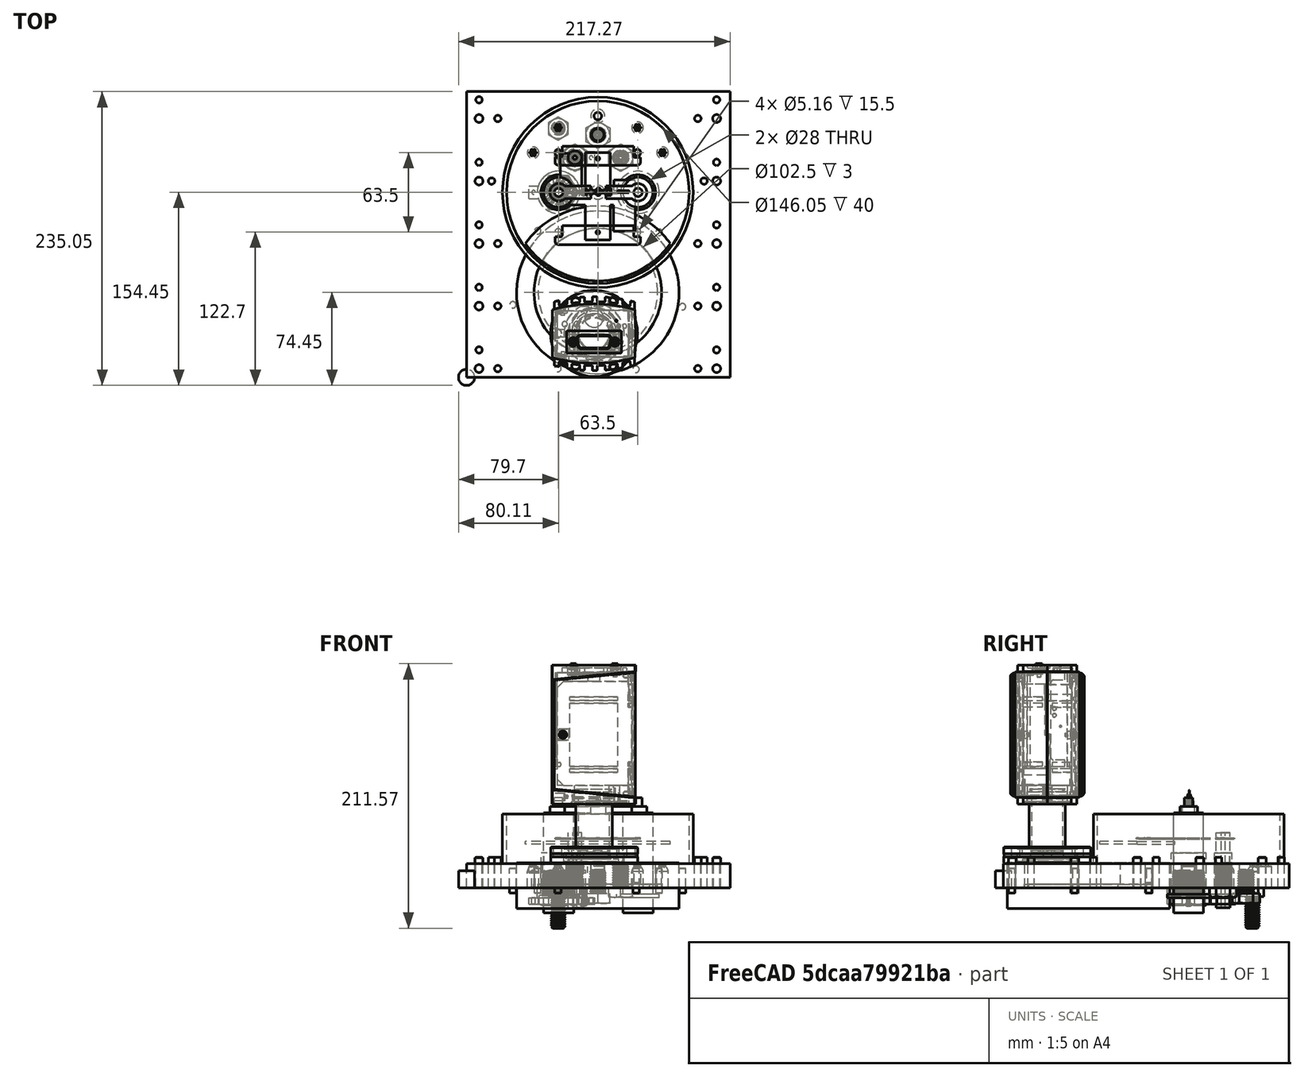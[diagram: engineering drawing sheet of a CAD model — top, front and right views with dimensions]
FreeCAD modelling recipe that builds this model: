
FCSTD DOCUMENT  (FreeCAD 0.17R13509 (Git))
Label: chamber_RF_new_feeds_sim
License: All rights reserved
LicenseURL: http://en.wikipedia.org/wiki/All_rights_reserved
objects: Part::Cylinder×125, Part::MultiFuse×48, Part::Box×24, Part::Cut×15, Part::Feature×8, Part::Fillet×6, Part::FeaturePython×5, Part::Sphere×4, Part::MultiCommon×2, Part::Cone×2
note: 239 computed .brp shape members not serialized (recipe doc carries the construction recipe); baked Part::Feature solids carry a one-line shape summary decoded from their .brp

FEATURE [Part::Box] Box  label="BasePlate"
  AttacherType = Attacher::AttachEngine3D
  Height = 19.5
  Length = 210.82
  Width = 228.6
  expr: Length = 8.3000000000000007 * 25.399999999999999
  expr: Width = 9 * 25.399999999999999
FEATURE [Part::Cylinder] Cylinder  label="Flange"
  Angle = 360
  AttacherType = Attacher::AttachEngine3D
  Height = 20
  Placement = pos=(105,68,0) rot=(0,0,1;0rad)
  Radius = 65
  expr: Placement.Base.x = 210 / 2
  expr: Radius = 130 / 2
FEATURE [Part::Cylinder] Cylinder001  label="TurboPumpInlet"
  Angle = 360
  AttacherType = Attacher::AttachEngine3D
  Height = 20
  Placement = pos=(105,68,0) rot=(0,0,1;0rad)
  Radius = 51
  expr: Placement.Base.x = 210 / 2
  expr: Radius = 102 / 2
FEATURE [Part::Cylinder] Cylinder002  label="ChamberWall"
  Angle = 360
  AttacherType = Attacher::AttachEngine3D
  Height = 40
  Placement = pos=(105,148,0) rot=(0,0,1;0rad)
  Radius = 76.2
  expr: Placement.Base.x = 210 / 2
  expr: Radius = 3 * 25.399999999999999
FEATURE [Part::Cylinder] Cylinder003  label="TurboPump"
  Angle = 360
  AttacherType = Attacher::AttachEngine3D
  Height = 16.4
  Placement = pos=(105,68,-16.4) rot=(0,0,1;0rad)
  Radius = 65
  expr: Placement.Base.x = 210 / 2
  expr: Radius = 130 / 2
FEATURE [Part::Cylinder] Cylinder004  label="Chamber001"
  Angle = 360
  AttacherType = Attacher::AttachEngine3D
  Height = 20
  Placement = pos=(105,148,0) rot=(0,0,1;0rad)
  Radius = 70.0875
  expr: Placement.Base.x = 210 / 2
  expr: Radius = 5.5625 * 25.199999999999999 / 2
FEATURE [Part::Cylinder] Cylinder005
  Angle = 360
  AttacherType = Attacher::AttachEngine3D
  Height = 20
  Placement = pos=(105,68,0) rot=(0,0,1;0rad)
  Radius = 51
  expr: Placement.Base.x = 210 / 2
  expr: Radius = 102 / 2
FEATURE [Part::MultiCommon] Common  label="Inlet"
  Shapes = -> [Cylinder004,Cylinder005]
FEATURE [Part::Cylinder] Cylinder012  label="Threaded"
  Angle = 360
  AttacherType = Attacher::AttachEngine3D
  Height = 19.5
  Placement = pos=(36.025,58.5,-4) rot=(0,0,1;0rad)
  Radius = 2.57969
  expr: Placement.Base.x = 105 - 68.674999999999997 - 0.29999999999999999
  expr: Radius = 13 / 64 * 25.399999999999999 / 2
FEATURE [Part::MultiFuse] Fusion
  Shapes = -> [Cylinder003,Cylinder001]
FEATURE [Part::Cylinder] Cylinder008  label="ChamberWall001"
  Angle = 360
  AttacherType = Attacher::AttachEngine3D
  Height = 40
  Placement = pos=(105,148,0) rot=(0,0,1;0rad)
  Radius = 73.025
  expr: Placement.Base.x = 210 / 2
  expr: Radius = (3 - 0.125) * 25.399999999999999
FEATURE [Part::Cut] Cut  label="ChamberWall002"
  Base = -> Cylinder002
  Placement = pos=(0,0,19) rot=(0,0,1;0rad)
  Tool = -> Cylinder008
FEATURE [Part::Cylinder] Cylinder013  label="Threaded001"
  Angle = 360
  AttacherType = Attacher::AttachEngine3D
  Height = 19.5
  Placement = pos=(136.75,179.75,4) rot=(0,0,1;0rad)
  Radius = 2.57969
  expr: Placement.Base.x = 105 + 31.75
  expr: Placement.Base.y = 148 + 31.75
  expr: Radius = 13 / 64 * 25.399999999999999 / 2
FEATURE [Part::Cylinder] Cylinder014  label="Threaded002"
  Angle = 360
  AttacherType = Attacher::AttachEngine3D
  Height = 19.5
  Placement = pos=(73.25,179.75,4) rot=(0,0,1;0rad)
  Radius = 2.57969
  expr: Placement.Base.x = 105 - 31.75
  expr: Placement.Base.y = 148 + 31.75
  expr: Radius = 13 / 64 * 25.399999999999999 / 2
FEATURE [Part::Cylinder] Cylinder015  label="Threaded003"
  Angle = 360
  AttacherType = Attacher::AttachEngine3D
  Height = 23.5
  Placement = pos=(73.25,116.25,4) rot=(0,0,1;0rad)
  Radius = 2.57969
  expr: Placement.Base.x = 105 - 31.75
  expr: Placement.Base.y = 148 - 31.75
  expr: Radius = 13 / 64 * 25.399999999999999 / 2
FEATURE [Part::Cylinder] Cylinder016  label="Threaded004"
  Angle = 360
  AttacherType = Attacher::AttachEngine3D
  Height = 23.5
  Placement = pos=(136.75,116.25,4) rot=(0,0,1;0rad)
  Radius = 2.57969
  expr: Placement.Base.x = 105 + 31.75
  expr: Placement.Base.y = 148 - 31.75
  expr: Radius = 13 / 64 * 25.399999999999999 / 2
FEATURE [Part::MultiFuse] Fusion003  label="Risers"
  Shapes = -> [Cylinder016,Cylinder015,Cylinder014,Cylinder013]
FEATURE [Part::Cylinder] Cylinder017  label="Unthreaded"
  Angle = 360
  AttacherType = Attacher::AttachEngine3D
  Height = 24
  Placement = pos=(10,10,0) rot=(0,0,1;0rad)
  Radius = 3.175
FEATURE [Part::FeaturePython] Array  label="TurboMounts"  # Draft array (typed FeaturePython)
  Angle = 270
  ArrayType = 1
  Axis = (0,0,1)
  Base = -> Cylinder012
  Center = (0,0,0)
  Fuse = false
  IntervalAxis = (0,0,0)
  IntervalX = (1,0,0)
  IntervalY = (0,1,0)
  IntervalZ = (0,0,0)
  NumberPolar = 6
  NumberX = 2
  NumberY = 2
  NumberZ = 1
  Placement = pos=(105,68,0) rot=(0,0,1;1.32645rad)
FEATURE [Part::Cylinder] Cylinder018  label="Threaded005"
  Angle = 360
  AttacherType = Attacher::AttachEngine3D
  Height = 24.5
  Placement = pos=(25,10,0) rot=(0,0,1;0rad)
  Radius = 2.57969
FEATURE [Part::Cylinder] Cylinder019  label="Unthreaded001"
  Angle = 360
  AttacherType = Attacher::AttachEngine3D
  Height = 24
  Placement = pos=(10,10,0) rot=(0,0,1;0rad)
  Radius = 3.175
FEATURE [Part::Cylinder] Cylinder020  label="Threaded006"
  Angle = 360
  AttacherType = Attacher::AttachEngine3D
  Height = 24.5
  Placement = pos=(-5,10,0) rot=(0,0,1;0rad)
  Radius = 2.57969
FEATURE [Part::Cylinder] Cylinder021  label="Threaded007"
  Angle = 360
  AttacherType = Attacher::AttachEngine3D
  Height = 24.5
  Placement = pos=(10,25,0) rot=(0,0,1;0rad)
  Radius = 2.57969
FEATURE [Part::MultiFuse] Fusion004  label="MountSet1"
  Shapes = -> [Cylinder021,Cylinder018,Cylinder017]
FEATURE [Part::Cylinder] Cylinder022  label="Threaded008"
  Angle = 360
  AttacherType = Attacher::AttachEngine3D
  Height = 24.5
  Placement = pos=(10,25,0) rot=(0,0,1;0rad)
  Radius = 2.57969
FEATURE [Part::MultiFuse] Fusion005  label="MountSet2"
  Placement = pos=(190,0,0) rot=(0,0,1;0rad)
  Shapes = -> [Cylinder022,Cylinder019,Cylinder020]
FEATURE [Part::MultiFuse] Fusion006  label="MountBar"
  Shapes = -> [Fusion005,Fusion004]
FEATURE [Part::Cylinder] Cylinder023  label="Unthreaded002"
  Angle = 360
  AttacherType = Attacher::AttachEngine3D
  Height = 24
  Placement = pos=(10,10,0) rot=(0,0,1;0rad)
  Radius = 3.175
FEATURE [Part::Cylinder] Cylinder024  label="Threaded009"
  Angle = 360
  AttacherType = Attacher::AttachEngine3D
  Height = 24.5
  Placement = pos=(25,10,0) rot=(0,0,1;0rad)
  Radius = 2.57969
FEATURE [Part::Cylinder] Cylinder025  label="Unthreaded003"
  Angle = 360
  AttacherType = Attacher::AttachEngine3D
  Height = 24
  Placement = pos=(10,10,0) rot=(0,0,1;0rad)
  Radius = 3.175
FEATURE [Part::Cylinder] Cylinder026  label="Threaded010"
  Angle = 360
  AttacherType = Attacher::AttachEngine3D
  Height = 24.5
  Placement = pos=(-5,10,0) rot=(0,0,1;0rad)
  Radius = 2.57969
FEATURE [Part::Cylinder] Cylinder027  label="Threaded011"
  Angle = 360
  AttacherType = Attacher::AttachEngine3D
  Height = 24.5
  Placement = pos=(10,25,0) rot=(0,0,1;0rad)
  Radius = 2.57969
FEATURE [Part::MultiFuse] Fusion007  label="MountSet003"
  Shapes = -> [Cylinder027,Cylinder024,Cylinder023]
FEATURE [Part::Cylinder] Cylinder028  label="Threaded012"
  Angle = 360
  AttacherType = Attacher::AttachEngine3D
  Height = 24.5
  Placement = pos=(10,25,0) rot=(0,0,1;0rad)
  Radius = 2.57969
FEATURE [Part::MultiFuse] Fusion008  label="MountSet004"
  Placement = pos=(190,0,0) rot=(0,0,1;0rad)
  Shapes = -> [Cylinder028,Cylinder025,Cylinder026]
FEATURE [Part::MultiFuse] Fusion009  label="MountBar001"
  Placement = pos=(0,50,0) rot=(0,0,1;0rad)
  Shapes = -> [Fusion008,Fusion007]
FEATURE [Part::Cylinder] Cylinder029  label="Unthreaded004"
  Angle = 360
  AttacherType = Attacher::AttachEngine3D
  Height = 24
  Placement = pos=(10,10,0) rot=(0,0,1;0rad)
  Radius = 3.175
FEATURE [Part::Cylinder] Cylinder030  label="Threaded013"
  Angle = 360
  AttacherType = Attacher::AttachEngine3D
  Height = 24.5
  Placement = pos=(25,10,0) rot=(0,0,1;0rad)
  Radius = 2.57969
FEATURE [Part::Cylinder] Cylinder031  label="Unthreaded005"
  Angle = 360
  AttacherType = Attacher::AttachEngine3D
  Height = 24
  Placement = pos=(10,10,0) rot=(0,0,1;0rad)
  Radius = 3.175
FEATURE [Part::Cylinder] Cylinder032  label="Threaded014"
  Angle = 360
  AttacherType = Attacher::AttachEngine3D
  Height = 24.5
  Placement = pos=(-5,10,0) rot=(0,0,1;0rad)
  Radius = 2.57969
FEATURE [Part::Cylinder] Cylinder033  label="Threaded015"
  Angle = 360
  AttacherType = Attacher::AttachEngine3D
  Height = 24.5
  Placement = pos=(10,25,0) rot=(0,0,1;0rad)
  Radius = 2.57969
FEATURE [Part::MultiFuse] Fusion010  label="MountSet005"
  Shapes = -> [Cylinder033,Cylinder030,Cylinder029]
FEATURE [Part::Cylinder] Cylinder034  label="Threaded016"
  Angle = 360
  AttacherType = Attacher::AttachEngine3D
  Height = 24.5
  Placement = pos=(10,25,0) rot=(0,0,1;0rad)
  Radius = 2.57969
FEATURE [Part::MultiFuse] Fusion011  label="MountSet006"
  Placement = pos=(190,0,0) rot=(0,0,1;0rad)
  Shapes = -> [Cylinder034,Cylinder031,Cylinder032]
FEATURE [Part::MultiFuse] Fusion012  label="MountBar002"
  Placement = pos=(0,100,0) rot=(0,0,1;0rad)
  Shapes = -> [Fusion011,Fusion010]
FEATURE [Part::Cylinder] Cylinder035  label="Unthreaded006"
  Angle = 360
  AttacherType = Attacher::AttachEngine3D
  Height = 24
  Placement = pos=(10,10,0) rot=(0,0,1;0rad)
  Radius = 3.175
FEATURE [Part::Cylinder] Cylinder036  label="Threaded017"
  Angle = 360
  AttacherType = Attacher::AttachEngine3D
  Height = 24.5
  Placement = pos=(20,10,0) rot=(0,0,1;0rad)
  Radius = 2.57969
FEATURE [Part::Cylinder] Cylinder037  label="Unthreaded007"
  Angle = 360
  AttacherType = Attacher::AttachEngine3D
  Height = 24
  Placement = pos=(10,10,0) rot=(0,0,1;0rad)
  Radius = 3.175
FEATURE [Part::Cylinder] Cylinder038  label="Threaded018"
  Angle = 360
  AttacherType = Attacher::AttachEngine3D
  Height = 24.5
  Placement = pos=(0,10,0) rot=(0,0,1;0rad)
  Radius = 2.57969
FEATURE [Part::Cylinder] Cylinder039  label="Threaded019"
  Angle = 360
  AttacherType = Attacher::AttachEngine3D
  Height = 24.5
  Placement = pos=(10,25,0) rot=(0,0,1;0rad)
  Radius = 2.57969
FEATURE [Part::MultiFuse] Fusion013  label="MountSet007"
  Shapes = -> [Cylinder039,Cylinder036,Cylinder035]
FEATURE [Part::Cylinder] Cylinder040  label="Threaded020"
  Angle = 360
  AttacherType = Attacher::AttachEngine3D
  Height = 24.5
  Placement = pos=(10,25,0) rot=(0,0,1;0rad)
  Radius = 2.57969
FEATURE [Part::MultiFuse] Fusion014  label="MountSet008"
  Placement = pos=(190,0,0) rot=(0,0,1;0rad)
  Shapes = -> [Cylinder040,Cylinder037,Cylinder038]
FEATURE [Part::MultiFuse] Fusion015  label="MountBar003"
  Placement = pos=(0,150,0) rot=(0,0,1;0rad)
  Shapes = -> [Fusion014,Fusion013]
FEATURE [Part::Cylinder] Cylinder041  label="Unthreaded008"
  Angle = 360
  AttacherType = Attacher::AttachEngine3D
  Height = 24
  Placement = pos=(10,10,0) rot=(0,0,1;0rad)
  Radius = 3.175
FEATURE [Part::Cylinder] Cylinder042  label="Threaded021"
  Angle = 360
  AttacherType = Attacher::AttachEngine3D
  Height = 24.5
  Placement = pos=(25,10,0) rot=(0,0,1;0rad)
  Radius = 2.57969
FEATURE [Part::Cylinder] Cylinder043  label="Unthreaded009"
  Angle = 360
  AttacherType = Attacher::AttachEngine3D
  Height = 24
  Placement = pos=(10,10,0) rot=(0,0,1;0rad)
  Radius = 3.175
FEATURE [Part::Cylinder] Cylinder044  label="Threaded022"
  Angle = 360
  AttacherType = Attacher::AttachEngine3D
  Height = 24.5
  Placement = pos=(-5,10,0) rot=(0,0,1;0rad)
  Radius = 2.57969
FEATURE [Part::Cylinder] Cylinder045  label="Threaded023"
  Angle = 360
  AttacherType = Attacher::AttachEngine3D
  Height = 24.5
  Placement = pos=(10,25,0) rot=(0,0,1;0rad)
  Radius = 2.57969
FEATURE [Part::MultiFuse] Fusion016  label="MountSet009"
  Shapes = -> [Cylinder045,Cylinder042,Cylinder041]
FEATURE [Part::Cylinder] Cylinder046  label="Threaded024"
  Angle = 360
  AttacherType = Attacher::AttachEngine3D
  Height = 24.5
  Placement = pos=(10,25,0) rot=(0,0,1;0rad)
  Radius = 2.57969
FEATURE [Part::MultiFuse] Fusion017  label="MountSet010"
  Placement = pos=(190,0,0) rot=(0,0,1;0rad)
  Shapes = -> [Cylinder046,Cylinder043,Cylinder044]
FEATURE [Part::MultiFuse] Fusion018  label="MountBar004"
  Placement = pos=(0,200,0) rot=(0,0,1;0rad)
  Shapes = -> [Fusion017,Fusion016]
FEATURE [Part::MultiFuse] Fusion019  label="MountSet"
  Placement = pos=(0,-3,0) rot=(0,0,1;0rad)
  Shapes = -> [Fusion018,Fusion015,Fusion012,Fusion009,Fusion006]
FEATURE [Part::Cylinder] Cylinder048  label="NPT1"
  Angle = 360
  AttacherType = Attacher::AttachEngine3D
  Height = 18
  Placement = pos=(105,148,0) rot=(0,0,1;0rad)
  Radius = 5.55625
  expr: Radius = 7 / 16 * 25.399999999999999 / 2
FEATURE [Part::Cylinder] Cylinder049  label="WireFT1"
  Angle = 360
  AttacherType = Attacher::AttachEngine3D
  Height = 13
  Radius = 4.56406
  expr: Radius = 23 / 64 * 25.399999999999999 / 2
FEATURE [Part::Cylinder] Cylinder051  label="Flange001"
  Angle = 360
  AttacherType = Attacher::AttachEngine3D
  Height = 3
  Placement = pos=(105,68,0) rot=(0,0,1;0rad)
  Radius = 51.25
  expr: Placement.Base.x = 210 / 2
  expr: Radius = 102.5 / 2
FEATURE [Part::Cylinder] Cylinder052  label="Flange002"
  Angle = 360
  AttacherType = Attacher::AttachEngine3D
  Height = 3
  Placement = pos=(105,68,0) rot=(0,0,1;0rad)
  Radius = 47.75
  expr: Placement.Base.x = 210 / 2
  expr: Radius = 51.25 - 3.5
FEATURE [Part::Cut] Cut001  label="CenteringRingGroove"
  Base = -> Cylinder051
  Tool = -> Cylinder052
FEATURE [Part::Cylinder] Cylinder053  label="NPT002"
  Angle = 360
  AttacherType = Attacher::AttachEngine3D
  Height = 17
  Placement = pos=(105,209,0) rot=(0,0,1;0rad)
  Radius = 5.55625
  expr: Radius = 7 / 16 * 25.399999999999999 / 2
FEATURE [Part::Cylinder] Cylinder054  label="WireHole"
  Angle = 360
  AttacherType = Attacher::AttachEngine3D
  Height = 28
  Placement = pos=(2,0,0) rot=(0,0,1;0rad)
  Radius = 0.79375
FEATURE [Part::FeaturePython] Array001  # Draft array (typed FeaturePython)
  Angle = 360
  ArrayType = 1
  Axis = (0,0,1)
  Base = -> Cylinder054
  Center = (0,0,0)
  Fuse = false
  IntervalAxis = (0,0,0)
  IntervalX = (1,0,0)
  IntervalY = (0,1,0)
  IntervalZ = (0,0,0)
  NumberPolar = 6
  NumberX = 2
  NumberY = 2
  NumberZ = 1
FEATURE [Part::Cylinder] Cylinder056  label="WireHole001"
  Angle = 360
  AttacherType = Attacher::AttachEngine3D
  Height = 28
  Radius = 0.79375
FEATURE [Part::MultiFuse] Fusion020  label="WireFT_Holes"
  Shapes = -> [Cylinder056,Array001]
FEATURE [Part::Cylinder] Cylinder058  label="WireFT003"
  Angle = 360
  AttacherType = Attacher::AttachEngine3D
  Height = 13
  Radius = 4.56406
  expr: Radius = 23 / 64 * 25.399999999999999 / 2
FEATURE [Part::Cylinder] Cylinder059  label="WireHole002"
  Angle = 360
  AttacherType = Attacher::AttachEngine3D
  Height = 28
  Placement = pos=(2,0,0) rot=(0,0,1;0rad)
  Radius = 0.79375
FEATURE [Part::FeaturePython] Array002  # Draft array (typed FeaturePython)
  Angle = 360
  ArrayType = 1
  Axis = (0,0,1)
  Base = -> Cylinder059
  Center = (0,0,0)
  Fuse = false
  IntervalAxis = (0,0,0)
  IntervalX = (1,0,0)
  IntervalY = (0,1,0)
  IntervalZ = (0,0,0)
  NumberPolar = 6
  NumberX = 2
  NumberY = 2
  NumberZ = 1
FEATURE [Part::Cylinder] Cylinder060  label="WireHole003"
  Angle = 360
  AttacherType = Attacher::AttachEngine3D
  Height = 28
  Radius = 0.79375
FEATURE [Part::MultiFuse] Fusion022  label="WireFT_Holes001"
  Shapes = -> [Cylinder060,Array002]
FEATURE [Part::Sphere] Sphere  label="Compression"
  Angle1 = -90
  Angle2 = 90
  Angle3 = 360
  AttacherType = Attacher::AttachEngine3D
  Placement = pos=(0,0,13) rot=(0,0,1;0rad)
  Radius = 4.56
FEATURE [Part::MultiFuse] Fusion024  label="WireFT"
  Placement = pos=(53.25,179.75,0) rot=(0,0,1;0rad)
  Shapes = -> [Sphere,Fusion020,Cylinder049]
  expr: Placement.Base.x = 73.25 - 20
FEATURE [Part::Sphere] Sphere001  label="Compression001"
  Angle1 = -90
  Angle2 = 90
  Angle3 = 360
  AttacherType = Attacher::AttachEngine3D
  Placement = pos=(0,0,13) rot=(0,0,1;0rad)
  Radius = 4.56
FEATURE [Part::MultiFuse] Fusion025  label="WireFT004"
  Placement = pos=(73.25,199.75,0) rot=(0,0,1;0rad)
  Shapes = -> [Cylinder058,Fusion022,Sphere001]
  expr: Placement.Base.y = 179.75 + 20
FEATURE [Part::Cylinder] Cylinder061  label="WireFT005"
  Angle = 360
  AttacherType = Attacher::AttachEngine3D
  Height = 13
  Radius = 4.56406
  expr: Radius = 23 / 64 * 25.399999999999999 / 2
FEATURE [Part::Cylinder] Cylinder062  label="WireHole004"
  Angle = 360
  AttacherType = Attacher::AttachEngine3D
  Height = 28
  Placement = pos=(2,0,0) rot=(0,0,1;0rad)
  Radius = 0.79375
FEATURE [Part::FeaturePython] Array003  # Draft array (typed FeaturePython)
  Angle = 360
  ArrayType = 1
  Axis = (0,0,1)
  Base = -> Cylinder062
  Center = (0,0,0)
  Fuse = false
  IntervalAxis = (0,0,0)
  IntervalX = (1,0,0)
  IntervalY = (0,1,0)
  IntervalZ = (0,0,0)
  NumberPolar = 6
  NumberX = 2
  NumberY = 2
  NumberZ = 1
FEATURE [Part::Cylinder] Cylinder063  label="WireHole005"
  Angle = 360
  AttacherType = Attacher::AttachEngine3D
  Height = 28
  Radius = 0.79375
FEATURE [Part::MultiFuse] Fusion026  label="WireFT_Holes002"
  Shapes = -> [Cylinder063,Array003]
FEATURE [Part::Sphere] Sphere002  label="Compression002"
  Angle1 = -90
  Angle2 = 90
  Angle3 = 360
  AttacherType = Attacher::AttachEngine3D
  Placement = pos=(0,0,13) rot=(0,0,1;0rad)
  Radius = 4.56
FEATURE [Part::MultiFuse] Fusion027  label="WireFT006"
  Placement = pos=(136.75,199.75,0) rot=(0,0,1;0rad)
  Shapes = -> [Cylinder061,Fusion026,Sphere002]
  expr: Placement.Base.y = 179.75 + 20
FEATURE [Part::Cylinder] Cylinder064  label="WireFT007"
  Angle = 360
  AttacherType = Attacher::AttachEngine3D
  Height = 13
  Radius = 4.56406
  expr: Radius = 23 / 64 * 25.399999999999999 / 2
FEATURE [Part::Cylinder] Cylinder065  label="WireHole006"
  Angle = 360
  AttacherType = Attacher::AttachEngine3D
  Height = 28
  Placement = pos=(2,0,0) rot=(0,0,1;0rad)
  Radius = 0.79375
FEATURE [Part::FeaturePython] Array004  # Draft array (typed FeaturePython)
  Angle = 360
  ArrayType = 1
  Axis = (0,0,1)
  Base = -> Cylinder065
  Center = (0,0,0)
  Fuse = false
  IntervalAxis = (0,0,0)
  IntervalX = (1,0,0)
  IntervalY = (0,1,0)
  IntervalZ = (0,0,0)
  NumberPolar = 6
  NumberX = 2
  NumberY = 2
  NumberZ = 1
FEATURE [Part::Cylinder] Cylinder066  label="WireHole007"
  Angle = 360
  AttacherType = Attacher::AttachEngine3D
  Height = 28
  Radius = 0.79375
FEATURE [Part::MultiFuse] Fusion028  label="WireFT_Holes003"
  Shapes = -> [Cylinder066,Array004]
FEATURE [Part::Sphere] Sphere003  label="Compression003"
  Angle1 = -90
  Angle2 = 90
  Angle3 = 360
  AttacherType = Attacher::AttachEngine3D
  Placement = pos=(0,0,13) rot=(0,0,1;0rad)
  Radius = 4.56
FEATURE [Part::MultiFuse] Fusion029  label="WireFT008"
  Placement = pos=(156.75,179.75,0) rot=(0,0,1;0rad)
  Shapes = -> [Cylinder064,Fusion028,Sphere003]
  expr: Placement.Base.x = 136.75 + 20
  expr: Placement.Base.y = 179.75
FEATURE [Part::Cylinder] Cylinder067  label="NPT002_inner"
  Angle = 360
  AttacherType = Attacher::AttachEngine3D
  Height = 23
  Placement = pos=(105,209,0) rot=(0,0,1;0rad)
  Radius = 3
  expr: Radius = 3
FEATURE [Part::Cylinder] Cylinder068  label="Cylinder"
  Angle = 360
  AttacherType = Attacher::AttachEngine3D
  Height = 2
  Placement = pos=(105,148,35) rot=(0,0,1;0rad)
  Radius = 71
FEATURE [Part::Cylinder] Cylinder069  label="Cylinder006"
  Angle = 360
  AttacherType = Attacher::AttachEngine3D
  Height = 2
  Placement = pos=(105,66,35) rot=(0,0,1;0rad)
  Radius = 71
FEATURE [Part::MultiCommon] Common001  label="BaffleDiff"
  Shapes = -> [Cylinder069,Cylinder068]
FEATURE [Part::Cylinder] Cylinder070  label="RFFeeds3"
  Angle = 360
  AttacherType = Attacher::AttachEngine3D
  Height = 20
  Placement = pos=(105,194,0) rot=(0,0,1;0rad)
  Radius = 5.35813
FEATURE [Part::Feature] Part__Feature  label="92941A710"
  Placement = pos=(86.69,175.69,6) rot=(0,-1,0;1.5708rad)
  shape: bbox 22 x 22 x 27.53 mm, 39 faces (baked)
  expr: Placement.Base.x = 105 - 18.309999999999999
  expr: Placement.Base.y = 194 - 18.309999999999999
FEATURE [Part::Feature] Part__Feature001  label="50785K338"
  Placement = pos=(73.66,148,0) rot=(0.707107,0.707107,0;3.14159rad)
  shape: bbox 31.16 x 31.16 x 28.81 mm, 49 faces (baked)
FEATURE [Part::Feature] Part__Feature002  label="92941A669"
  Placement = pos=(73.25,199,-16) rot=(0,1,0;1.5708rad)
  shape: bbox 18.33 x 18.33 x 33.04 mm, 48 faces (baked)
FEATURE [Part::Feature] Part__Feature003  label="92941A711"
  Placement = pos=(123.31,175.69,6) rot=(0,-1,0;1.5708rad)
  shape: bbox 22 x 22 x 27.53 mm, 39 faces (baked)
  expr: Placement.Base.x = 105 + 18.309999999999999
  expr: Placement.Base.y = 194 - 18.309999999999999
FEATURE [Part::Feature] Part__Feature004  label="92941A712"
  Placement = pos=(105,194,1) rot=(0,-1,0;1.5708rad)
  shape: bbox 22 x 22 x 27.53 mm, 39 faces (baked)
FEATURE [Part::Cylinder] Cylinder071  label="RFFeeds1"
  Angle = 360
  AttacherType = Attacher::AttachEngine3D
  Height = 33
  Placement = pos=(86.69,175.69,-5) rot=(0,0,1;0rad)
  Radius = 7
  expr: Placement.Base.x = 105 - 18.309999999999999
  expr: Placement.Base.y = 194 - 18.309999999999999
FEATURE [Part::Cylinder] Cylinder072  label="RFFeeds2"
  Angle = 360
  AttacherType = Attacher::AttachEngine3D
  Height = 20
  Placement = pos=(123.31,175.69,0) rot=(0,0,1;0rad)
  Radius = 5.35813
  expr: Placement.Base.x = 105 + 18.309999999999999
  expr: Placement.Base.y = 194 - 18.309999999999999
FEATURE [Part::Box] Box001  label="ShieldCross1"
  AttacherType = Attacher::AttachEngine3D
  Height = 1.01
  Length = 68
  Placement = pos=(71,169.75,39) rot=(0,0,1;0rad)
  Width = 15
  expr: Placement.Base.y = 179.75 - 20 / 2
  expr: Placement.Base.x = 105 - 68 / 2
FEATURE [Part::Cylinder] Cylinder073  label="Threaded025"
  Angle = 360
  AttacherType = Attacher::AttachEngine3D
  Height = 56.5
  Placement = pos=(73.25,179.75,4) rot=(0,0,1;0rad)
  Radius = 2.57969
  expr: Placement.Base.x = 105 - 31.75
  expr: Placement.Base.y = 148 + 31.75
  expr: Radius = 13 / 64 * 25.399999999999999 / 2
FEATURE [Part::Cylinder] Cylinder074  label="Threaded026"
  Angle = 360
  AttacherType = Attacher::AttachEngine3D
  Height = 55.5
  Placement = pos=(136.75,179.75,4) rot=(0,0,1;0rad)
  Radius = 2.57969
  expr: Placement.Base.x = 105 + 31.75
  expr: Placement.Base.y = 148 + 31.75
  expr: Radius = 13 / 64 * 25.399999999999999 / 2
FEATURE [Part::Fillet] Fillet
  Base = -> Box001
  Edges = 4 edges r=2: [Edge1,Edge3,Edge5,Edge7]
FEATURE [Part::Box] Box002  label="Cube"
  AttacherType = Attacher::AttachEngine3D
  Height = 10
  Length = 6.35
  Placement = pos=(70.075,175.825,36) rot=(0,0,1;0rad)
  Width = 15
  expr: Placement.Base.y = 179 - 6.3499999999999996 / 2
  expr: Placement.Base.x = 73.25 - 6.3499999999999996 / 2
FEATURE [Part::Fillet] Fillet001
  Base = -> Box002
  Edges = 2 edges r=1: [Edge1,Edge5]
FEATURE [Part::Box] Box003  label="Cube001"
  AttacherType = Attacher::AttachEngine3D
  Height = 10
  Length = 6.35
  Placement = pos=(70.075,175.825,36) rot=(0,0,1;0rad)
  Width = 15
  expr: Placement.Base.y = 179 - 6.3499999999999996 / 2
  expr: Placement.Base.x = 73.25 - 6.3499999999999996 / 2
FEATURE [Part::Fillet] Fillet002
  Base = -> Box003
  Edges = 2 edges r=1: [Edge1,Edge5]
  Placement = pos=(63.5,0,0) rot=(0,0,1;0rad)
  expr: Placement.Base.x = 136.75 - 73.25
FEATURE [Part::MultiFuse] Fusion032
  Shapes = -> [Fillet001,Cylinder073,Cylinder074,Fillet002]
FEATURE [Part::Cut] Cut003  label="ShieldBar2"
  Base = -> Fillet
  Tool = -> Fusion032
FEATURE [Part::Box] Box004  label="ShieldCross002"
  AttacherType = Attacher::AttachEngine3D
  Height = 1.01
  Length = 68
  Placement = pos=(71,169.75,39) rot=(0,0,1;0rad)
  Width = 15
  expr: Placement.Base.y = 179.75 - 20 / 2
  expr: Placement.Base.x = 105 - 68 / 2
FEATURE [Part::Cylinder] Cylinder075  label="Threaded027"
  Angle = 360
  AttacherType = Attacher::AttachEngine3D
  Height = 56.5
  Placement = pos=(73.25,179.75,4) rot=(0,0,1;0rad)
  Radius = 2.57969
  expr: Placement.Base.x = 105 - 31.75
  expr: Placement.Base.y = 148 + 31.75
  expr: Radius = 13 / 64 * 25.399999999999999 / 2
FEATURE [Part::Cylinder] Cylinder076  label="Threaded028"
  Angle = 360
  AttacherType = Attacher::AttachEngine3D
  Height = 55.5
  Placement = pos=(136.75,179.75,4) rot=(0,0,1;0rad)
  Radius = 2.57969
  expr: Placement.Base.x = 105 + 31.75
  expr: Placement.Base.y = 148 + 31.75
  expr: Radius = 13 / 64 * 25.399999999999999 / 2
FEATURE [Part::Fillet] Fillet003
  Base = -> Box004
  Edges = 4 edges r=2: [Edge1,Edge3,Edge5,Edge7]
FEATURE [Part::Box] Box005  label="Cube002"
  AttacherType = Attacher::AttachEngine3D
  Height = 10
  Length = 6.35
  Placement = pos=(70.075,175.825,36) rot=(0,0,1;0rad)
  Width = 15
  expr: Placement.Base.y = 179 - 6.3499999999999996 / 2
  expr: Placement.Base.x = 73.25 - 6.3499999999999996 / 2
FEATURE [Part::Fillet] Fillet004
  Base = -> Box005
  Edges = 2 edges r=1: [Edge1,Edge5]
FEATURE [Part::Box] Box006  label="Cube003"
  AttacherType = Attacher::AttachEngine3D
  Height = 10
  Length = 6.35
  Placement = pos=(70.075,175.825,36) rot=(0,0,1;0rad)
  Width = 15
  expr: Placement.Base.y = 179 - 6.3499999999999996 / 2
  expr: Placement.Base.x = 73.25 - 6.3499999999999996 / 2
FEATURE [Part::Fillet] Fillet005
  Base = -> Box006
  Edges = 2 edges r=1: [Edge1,Edge5]
  Placement = pos=(63.5,0,0) rot=(0,0,1;0rad)
  expr: Placement.Base.x = 136.75 - 73.25
FEATURE [Part::MultiFuse] Fusion033
  Shapes = -> [Fillet004,Cylinder075,Cylinder076,Fillet005]
FEATURE [Part::Cut] Cut004  label="ShieldBar1"
  Base = -> Fillet003
  Placement = pos=(0,-63.5,0) rot=(0,0,1;0rad)
  Tool = -> Fusion033
  expr: Placement.Base.y = 116.25 - 179.75
FEATURE [Part::Box] Box007  label="ShieldCross003"
  AttacherType = Attacher::AttachEngine3D
  Height = 1.01
  Length = 20
  Placement = pos=(95,109.75,39) rot=(0,0,1;0rad)
  Width = 70
  expr: Placement.Base.y = 179.75 - 70
  expr: Placement.Base.x = 105 - 10
FEATURE [Part::Box] Box008  label="ShieldCross004"
  AttacherType = Attacher::AttachEngine3D
  Height = 1.01
  Length = 20
  Placement = pos=(115,138,39) rot=(0,0,1;0rad)
  Width = 20
  expr: Placement.Base.y = 148 - 10
  expr: Placement.Base.x = 105 + 10
FEATURE [Part::Box] Box009  label="ShieldCross005"
  AttacherType = Attacher::AttachEngine3D
  Height = 1.01
  Length = 20
  Placement = pos=(75,138,39) rot=(0,0,1;0rad)
  Width = 20
  expr: Placement.Base.y = 148 - 10
  expr: Placement.Base.x = 105 - 30
FEATURE [Part::Box] Box010  label="ShieldCross006"
  AttacherType = Attacher::AttachEngine3D
  Height = 1.01
  Length = 17.5
  Placement = pos=(75,158,39) rot=(0,0,1;0rad)
  Width = 21
  expr: Placement.Base.y = 148 + 10
  expr: Placement.Base.x = 105 - 30
FEATURE [Part::Box] Box011  label="ShieldCross007"
  AttacherType = Attacher::AttachEngine3D
  Height = 1.01
  Length = 17.5
  Placement = pos=(117.5,117,39) rot=(0,0,1;0rad)
  Width = 21
  expr: Placement.Base.y = 148 - 31
  expr: Placement.Base.x = 105 + 12.5
FEATURE [Part::Cylinder] Cylinder077  label="ShieldCrossHole2"
  Angle = 360
  AttacherType = Attacher::AttachEngine3D
  Height = 10
  Placement = pos=(105,175,34) rot=(0,0,1;0rad)
  Radius = 1.5
FEATURE [Part::Cylinder] Cylinder078  label="ShieldCrossHole1"
  Angle = 360
  AttacherType = Attacher::AttachEngine3D
  Height = 10
  Placement = pos=(105,116,34) rot=(0,0,1;0rad)
  Radius = 1.5
FEATURE [Part::MultiFuse] Fusion036
  Shapes = -> [Box010,Box011,Box009,Box008,Box007]
FEATURE [Part::Cylinder] Cylinder079  label="ShieldCrossHole003"
  Angle = 360
  AttacherType = Attacher::AttachEngine3D
  Height = 10
  Placement = pos=(105,175,34) rot=(0,0,1;0rad)
  Radius = 1.5
FEATURE [Part::Cylinder] Cylinder080  label="ShieldCrossHole004"
  Angle = 360
  AttacherType = Attacher::AttachEngine3D
  Height = 10
  Placement = pos=(105,116,34) rot=(0,0,1;0rad)
  Radius = 1.5
FEATURE [Part::Cut] Cut006  label="ShieldBar003"
  Base = -> Cut004
  Tool = -> Cylinder080
FEATURE [Part::Cut] Cut007  label="ShieldBar4"
  Base = -> Cut003
  Tool = -> Cylinder079
FEATURE [Part::Box] Box012  label="Cube004"
  AttacherType = Attacher::AttachEngine3D
  Height = 10
  Length = 2.75
  Placement = pos=(92.25,146.75,34) rot=(0,0,1;0rad)
  Width = 34
FEATURE [Part::Box] Box013  label="Cube005"
  AttacherType = Attacher::AttachEngine3D
  Height = 10
  Length = 5.75
  Placement = pos=(89.25,146.625,34) rot=(0,0,1;0rad)
  Width = 2.75
  expr: Placement.Base.y = 148 - 2.75 / 2
FEATURE [Part::Box] Box014  label="Cube006"
  AttacherType = Attacher::AttachEngine3D
  Height = 10
  Length = 2.75
  Placement = pos=(115,146.75,34) rot=(0,0,1;0rad)
  Width = 34
FEATURE [Part::Box] Box015  label="Cube007"
  AttacherType = Attacher::AttachEngine3D
  Height = 10
  Length = 5.75
  Placement = pos=(115,146.625,34) rot=(0,0,1;0rad)
  Width = 2.75
  expr: Placement.Base.y = 148 - 2.75 / 2
FEATURE [Part::MultiFuse] Fusion037  label="ShieldCuts"
  Shapes = -> [Cylinder077,Cylinder078,Box015,Box014,Box013,Box012]
FEATURE [Part::Cut] Cut009  label="ShieldFold"
  Base = -> Fusion036
  Tool = -> Fusion037
FEATURE [Part::Cylinder] Cylinder082  label="FTHole2"
  Angle = 360
  AttacherType = Attacher::AttachEngine3D
  Height = 20
  Placement = pos=(137.16,148,0) rot=(0,0,1;0rad)
  Radius = 14
  expr: Radius = 28 / 2
  expr: Placement.Base.x = 210.81999999999999 / 2 + 31.75
FEATURE [Part::Cylinder] Cylinder083  label="FTHole1"
  Angle = 360
  AttacherType = Attacher::AttachEngine3D
  Height = 20
  Placement = pos=(73.66,148,0) rot=(0,0,1;0rad)
  Radius = 14
  expr: Radius = 28 / 2
  expr: Placement.Base.x = 210.81999999999999 / 2 - 31.75
FEATURE [Part::Cylinder] Cylinder084  label="Feedthrough005"
  Angle = 360
  AttacherType = Attacher::AttachEngine3D
  Height = 5
  Placement = pos=(73.66,148,-10) rot=(0,0,1;0rad)
  Radius = 17
  expr: Radius = 17
  expr: Placement.Base.x = 210.81999999999999 / 2 - 31.75
FEATURE [Part::Cylinder] Cylinder088  label="Feedthrough008"
  Angle = 360
  AttacherType = Attacher::AttachEngine3D
  Height = 33
  Placement = pos=(73.66,148,-10) rot=(0,0,1;0rad)
  Radius = 14
  expr: Radius = 28 / 2
  expr: Placement.Base.x = 210.81999999999999 / 2 - 31.75
FEATURE [Part::Cylinder] Cylinder090  label="FTInsInnerHole"
  Angle = 360
  AttacherType = Attacher::AttachEngine3D
  Height = 33
  Placement = pos=(73.66,148,-10) rot=(0,0,1;0rad)
  Radius = 11.7
  expr: Placement.Base.x = 210.81999999999999 / 2 - 31.75
FEATURE [Part::Box] Box016  label="FTInsLug"
  AttacherType = Attacher::AttachEngine3D
  Height = 5
  Length = 47
  Placement = pos=(50,143,7) rot=(0,0,1;0rad)
  Width = 10
FEATURE [Part::Cylinder] Cylinder091  label="FTThreaded2"
  Angle = 360
  AttacherType = Attacher::AttachEngine3D
  Height = 14
  Placement = pos=(53.66,148,0) rot=(0,0,1;0rad)
  Radius = 1.5
  expr: Placement.Base.x = 73.659999999999997 - 20
FEATURE [Part::Feature] Part__Feature005  label="91772A110"
  Placement = pos=(78.69,175.69,11) rot=(1,0,0;3.14159rad)
  shape: bbox 6.021 x 6.021 x 15.01 mm, 152 faces (baked)
  expr: Placement.Base.x = 86.689999999999998 - 8
FEATURE [Part::Feature] Part__Feature006  label="91772A111"
  Placement = pos=(93.66,148,0) rot=(1,0,0;3.14159rad)
  shape: bbox 6.021 x 6.021 x 15.01 mm, 152 faces (baked)
  expr: Placement.Base.x = 73.659999999999997 + 20
FEATURE [Part::Cylinder] Cylinder092  label="FTThreaded1"
  Angle = 360
  AttacherType = Attacher::AttachEngine3D
  Height = 14
  Placement = pos=(93.66,148,0) rot=(0,0,1;0rad)
  Radius = 1.5
  expr: Placement.Base.x = 73.659999999999997 + 20
FEATURE [Part::Cylinder] Cylinder093  label="FTInsMount1"
  Angle = 360
  AttacherType = Attacher::AttachEngine3D
  Height = 14
  Placement = pos=(53.66,148,-15) rot=(0,0,1;0rad)
  Radius = 1.5
  expr: Placement.Base.x = 73.659999999999997 - 20
FEATURE [Part::Cylinder] Cylinder094  label="FTInsMount2"
  Angle = 360
  AttacherType = Attacher::AttachEngine3D
  Height = 14
  Placement = pos=(93.66,148,-14) rot=(0,0,1;0rad)
  Radius = 1.5
  expr: Placement.Base.x = 73.659999999999997 + 20
FEATURE [Part::MultiFuse] Fusion038
  Shapes = -> [Cylinder084,Cylinder088,Box016]
FEATURE [Part::MultiFuse] Fusion039
  Shapes = -> [Cylinder094,Cylinder093,Cylinder090]
FEATURE [Part::Cut] Cut010  label="FTInsulator1"
  Base = -> Fusion038
  Placement = pos=(0,0,5) rot=(0,0,1;0rad)
  Tool = -> Fusion039
FEATURE [Part::MultiFuse] Fusion040  label="FTInsulatorMount1"
  Shapes = -> [Cylinder092,Cylinder091]
FEATURE [Part::Cylinder] Cylinder095  label="FT1bar"
  Angle = 360
  AttacherType = Attacher::AttachEngine3D
  Height = 80
  Placement = pos=(73.66,148,-20) rot=(0,0,1;0rad)
  Radius = 12
FEATURE [Part::Cylinder] Cylinder096  label="Feedthrough009"
  Angle = 360
  AttacherType = Attacher::AttachEngine3D
  Height = 5
  Placement = pos=(73.66,148,-10) rot=(0,0,1;0rad)
  Radius = 17
  expr: Radius = 17
  expr: Placement.Base.x = 210.81999999999999 / 2 - 31.75
FEATURE [Part::Box] Box017  label="FTInsLug001"
  AttacherType = Attacher::AttachEngine3D
  Height = 5
  Length = 47
  Placement = pos=(50,143,-10) rot=(0,0,1;0rad)
  Width = 10
FEATURE [Part::Cylinder] Cylinder097  label="FTInsInnerHole002"
  Angle = 360
  AttacherType = Attacher::AttachEngine3D
  Height = 33
  Placement = pos=(73.66,148,-10) rot=(0,0,1;0rad)
  Radius = 12
  expr: Placement.Base.x = 210.81999999999999 / 2 - 31.75
FEATURE [Part::Cylinder] Cylinder098  label="FTInsMount003"
  Angle = 360
  AttacherType = Attacher::AttachEngine3D
  Height = 14
  Placement = pos=(53.66,148,-15) rot=(0,0,1;0rad)
  Radius = 1.5
  expr: Placement.Base.x = 73.659999999999997 - 20
FEATURE [Part::Cylinder] Cylinder099  label="FTInsMount004"
  Angle = 360
  AttacherType = Attacher::AttachEngine3D
  Height = 14
  Placement = pos=(93.66,148,-14) rot=(0,0,1;0rad)
  Radius = 1.5
  expr: Placement.Base.x = 73.659999999999997 + 20
FEATURE [Part::MultiFuse] Fusion041
  Shapes = -> [Cylinder099,Cylinder098,Cylinder097]
FEATURE [Part::MultiFuse] Fusion042
  Shapes = -> [Cylinder096,Box017]
FEATURE [Part::Cut] Cut011  label="FTInsBackplate"
  Base = -> Fusion042
  Placement = pos=(0,0,-3) rot=(0,0,1;0rad)
  Tool = -> Fusion041
FEATURE [Part::Cylinder] Cylinder100  label="FT1flange"
  Angle = 360
  AttacherType = Attacher::AttachEngine3D
  Height = 3
  Placement = pos=(73.66,148,-8) rot=(0,0,1;0rad)
  Radius = 17
  expr: Placement.Base.x = 210.81999999999999 / 2 - 31.75
FEATURE [Part::MultiFuse] Fusion043  label="FT1"
  Shapes = -> [Cylinder095,Cylinder100]
FEATURE [Part::Cylinder] Cylinder101  label="RFFeeds004"
  Angle = 360
  AttacherType = Attacher::AttachEngine3D
  Height = 20
  Placement = pos=(86.69,175.69,0) rot=(0,0,1;0rad)
  Radius = 7
  expr: Placement.Base.x = 105 - 18.309999999999999
  expr: Placement.Base.y = 194 - 18.309999999999999
FEATURE [Part::Cylinder] Cylinder102  label="RFFeeds005"
  Angle = 360
  AttacherType = Attacher::AttachEngine3D
  Height = 5
  Placement = pos=(86.69,175.69,-5) rot=(0,0,1;0rad)
  Radius = 10
  expr: Placement.Base.x = 105 - 18.309999999999999
  expr: Placement.Base.y = 194 - 18.309999999999999
FEATURE [Part::Cylinder] Cylinder103  label="FTThreaded003"
  Angle = 360
  AttacherType = Attacher::AttachEngine3D
  Height = 11
  Placement = pos=(99.69,175.69,0) rot=(0,0,1;0rad)
  Radius = 1.5
FEATURE [Part::Cylinder] Cylinder104  label="RFFeeds006"
  Angle = 360
  AttacherType = Attacher::AttachEngine3D
  Height = 46
  Placement = pos=(86.69,175.69,-14) rot=(0,0,1;0rad)
  Radius = 5.2
  expr: Placement.Base.x = 105 - 18.309999999999999
  expr: Placement.Base.y = 194 - 18.309999999999999
FEATURE [Part::Cylinder] Cylinder105  label="RFFTrod1"
  Angle = 360
  AttacherType = Attacher::AttachEngine3D
  Height = 60
  Placement = pos=(86.69,175.69,-16) rot=(0,0,1;0rad)
  Radius = 5.5
  expr: Placement.Base.x = 105 - 18.309999999999999
  expr: Placement.Base.y = 194 - 18.309999999999999
FEATURE [Part::Cylinder] Cylinder106  label="RFcoolingHole"
  Angle = 360
  AttacherType = Attacher::AttachEngine3D
  Height = 108
  Placement = pos=(86.69,175.69,-20) rot=(0,0,1;0rad)
  Radius = 1.5
  expr: Placement.Base.x = 105 - 18.309999999999999
  expr: Placement.Base.y = 194 - 18.309999999999999
FEATURE [Part::Cylinder] Cylinder107  label="FTThreaded004"
  Angle = 360
  AttacherType = Attacher::AttachEngine3D
  Height = 11
  Placement = pos=(73.69,175.69,0) rot=(0,0,1;0rad)
  Radius = 1.5
FEATURE [Part::Cylinder] Cylinder108  label="RFFTrod002"
  Angle = 360
  AttacherType = Attacher::AttachEngine3D
  Height = 3
  Placement = pos=(86.69,175.69,-8) rot=(0,0,1;0rad)
  Radius = 9.5
  expr: Placement.Base.x = 105 - 18.309999999999999
  expr: Placement.Base.y = 194 - 18.309999999999999
FEATURE [Part::Box] Box018  label="RFFeedLug"
  AttacherType = Attacher::AttachEngine3D
  Height = 5
  Length = 14
  Placement = pos=(77.69,171.69,-5) rot=(0,0,1;0rad)
  Width = 1
FEATURE [Part::Cylinder] Cylinder109  label="FTThreaded005"
  Angle = 360
  AttacherType = Attacher::AttachEngine3D
  Height = 11
  Placement = pos=(73.69,175.69,-10) rot=(0,0,1;0rad)
  Radius = 1.5
FEATURE [Part::Cylinder] Cylinder110  label="FTThreaded006"
  Angle = 360
  AttacherType = Attacher::AttachEngine3D
  Height = 11
  Placement = pos=(99.69,175.69,-10) rot=(0,0,1;0rad)
  Radius = 1.5
FEATURE [Part::MultiFuse] Fusion044
  Shapes = -> [Cylinder108,Cylinder105]
FEATURE [Part::Cut] Cut012  label="RFFeed1"
  Base = -> Fusion044
  Tool = -> Cylinder106
FEATURE [Part::MultiFuse] Fusion045
  Shapes = -> [Cylinder071,Box018,Cylinder102]
FEATURE [Part::MultiFuse] Fusion046
  Shapes = -> [Cylinder109,Cylinder110,Cylinder104]
FEATURE [Part::Cut] Cut013  label="RFFTInsulator1"
  Base = -> Fusion045
  Tool = -> Fusion046
FEATURE [Part::MultiFuse] Fusion047  label="RFFTMounts1"
  Shapes = -> [Cylinder107,Cylinder103]
FEATURE [Part::Cylinder] Cylinder111  label="RFFeeds007"
  Angle = 360
  AttacherType = Attacher::AttachEngine3D
  Height = 5
  Placement = pos=(86.69,175.69,-5) rot=(0,0,1;0rad)
  Radius = 7
  expr: Placement.Base.x = 105 - 18.309999999999999
  expr: Placement.Base.y = 194 - 18.309999999999999
FEATURE [Part::Cylinder] Cylinder112  label="RFFeeds008"
  Angle = 360
  AttacherType = Attacher::AttachEngine3D
  Height = 5
  Placement = pos=(86.69,175.69,-5) rot=(0,0,1;0rad)
  Radius = 10
  expr: Placement.Base.x = 105 - 18.309999999999999
  expr: Placement.Base.y = 194 - 18.309999999999999
FEATURE [Part::Cylinder] Cylinder113  label="RFFeeds009"
  Angle = 360
  AttacherType = Attacher::AttachEngine3D
  Height = 46
  Placement = pos=(86.69,175.69,-14) rot=(0,0,1;0rad)
  Radius = 5.5
  expr: Placement.Base.x = 105 - 18.309999999999999
  expr: Placement.Base.y = 194 - 18.309999999999999
FEATURE [Part::Box] Box019  label="RFFeedLug001"
  AttacherType = Attacher::AttachEngine3D
  Height = 5
  Length = 32
  Placement = pos=(70.69,170.69,-5) rot=(0,0,1;0rad)
  Width = 10
FEATURE [Part::Cylinder] Cylinder114  label="FTThreaded007"
  Angle = 360
  AttacherType = Attacher::AttachEngine3D
  Height = 11
  Placement = pos=(73.69,175.69,-10) rot=(0,0,1;0rad)
  Radius = 1.5
FEATURE [Part::Cylinder] Cylinder115  label="FTThreaded008"
  Angle = 360
  AttacherType = Attacher::AttachEngine3D
  Height = 11
  Placement = pos=(99.69,175.69,-10) rot=(0,0,1;0rad)
  Radius = 1.5
FEATURE [Part::MultiFuse] Fusion048
  Shapes = -> [Cylinder111,Box019,Cylinder112]
FEATURE [Part::MultiFuse] Fusion049
  Shapes = -> [Cylinder114,Cylinder115,Cylinder113]
FEATURE [Part::Cut] Cut014  label="RFFTBackplate"
  Base = -> Fusion048
  Placement = pos=(0,0,-8) rot=(0,0,1;0rad)
  Tool = -> Fusion049
FEATURE [Part::Box] Box020  label="BowTieBar1"
  AttacherType = Attacher::AttachEngine3D
  Height = 5
  Length = 25.75
  Placement = pos=(73.66,143,60) rot=(0,0,1;0rad)
  Width = 10
  expr: Length = 63.5 / 2 - 10 + 4
  expr: Placement.Base.x = 73.659999999999997
FEATURE [Part::Cylinder] Cylinder116  label="BowTieBarRound1"
  Angle = 360
  AttacherType = Attacher::AttachEngine3D
  Height = 5
  Placement = pos=(73.66,148,60) rot=(0,0,1;0rad)
  Radius = 7
  expr: Placement.Base.x = 210.81999999999999 / 2 - 31.75
FEATURE [Part::Cylinder] Cylinder117  label="BowTieBarMount003"
  Angle = 360
  AttacherType = Attacher::AttachEngine3D
  Height = 9
  Placement = pos=(73.66,148,63) rot=(0,0,1;0rad)
  Radius = 3.35
  expr: Radius = 6.7000000000000002 / 2
  expr: Placement.Base.x = 210.81999999999999 / 2 - 31.75
FEATURE [Part::Box] Box021  label="BowTie1"
  AttacherType = Attacher::AttachEngine3D
  Height = 4.5
  Length = 20
  Placement = pos=(112,145.5,65) rot=(0,0,1;0rad)
  Width = 6
FEATURE [Part::Cylinder] Cylinder118  label="BowTieCrucibleHole"
  Angle = 360
  AttacherType = Attacher::AttachEngine3D
  Height = 8
  Placement = pos=(122,148.5,66) rot=(0,0,1;0rad)
  Radius = 1.5
FEATURE [Part::Cylinder] Cylinder119  label="BowTieMount1"
  Angle = 360
  AttacherType = Attacher::AttachEngine3D
  Height = 8
  Placement = pos=(114,151,63) rot=(0,0,1;0rad)
  Radius = 1.5
  expr: Radius = 3 / 2
FEATURE [Part::Cylinder] Cylinder120  label="BowTieMount002"
  Angle = 360
  AttacherType = Attacher::AttachEngine3D
  Height = 8
  Placement = pos=(130,148.5,63) rot=(0,0,1;0rad)
  Radius = 1.5
  expr: Radius = 3 / 2
FEATURE [Part::Cylinder] Cylinder121  label="BowTieCut1"
  Angle = 360
  AttacherType = Attacher::AttachEngine3D
  Height = 8
  Placement = pos=(125.5,145,64) rot=(0,0,1;0rad)
  Radius = 2.5
FEATURE [Part::Cylinder] Cylinder122  label="BowTieCut2"
  Angle = 360
  AttacherType = Attacher::AttachEngine3D
  Height = 8
  Placement = pos=(125.5,152,64) rot=(0,0,1;0rad)
  Radius = 2.5
FEATURE [Part::Cylinder] Cylinder123  label="BowTieCut3"
  Angle = 360
  AttacherType = Attacher::AttachEngine3D
  Height = 8
  Placement = pos=(118.5,152,64) rot=(0,0,1;0rad)
  Radius = 2.5
FEATURE [Part::Cylinder] Cylinder124  label="BowTieCut4"
  Angle = 360
  AttacherType = Attacher::AttachEngine3D
  Height = 8
  Placement = pos=(118.5,144.5,64) rot=(0,0,1;0rad)
  Radius = 2.5
FEATURE [Part::Cylinder] Cylinder126  label="BowTieNozzleCut"
  Angle = 360
  AttacherType = Attacher::AttachEngine3D
  Height = 5
  Placement = pos=(122,148.5,68.5) rot=(0,0,1;0rad)
  Radius = 2.1
FEATURE [Part::Cylinder] Cylinder127  label="BowTieMount007"
  Angle = 360
  AttacherType = Attacher::AttachEngine3D
  Height = 8
  Placement = pos=(114,146,63) rot=(0,0,1;0rad)
  Radius = 1.5
  expr: Radius = 3 / 2
FEATURE [Part::Box] Box023  label="BowTieCut5"
  AttacherType = Attacher::AttachEngine3D
  Height = 4.5
  Length = 3
  Placement = pos=(125,145.5,73) rot=(0,0,1;0rad)
  Width = 6
FEATURE [Part::Cylinder] Cylinder128  label="BowTieInjector"
  Angle = 360
  AttacherType = Attacher::AttachEngine3D
  Height = 9
  Placement = pos=(112,148.5,68) rot=(0,1,0;1.5708rad)
  Radius = 0.4
  expr: Radius = 0.80000000000000004 / 2
FEATURE [Part::MultiFuse] Fusion050
  Shapes = -> [Cylinder120,Cylinder119,Cylinder121,Cylinder122,Cylinder123,Cylinder124,Cylinder126,Cylinder118,Cylinder128,Box023,Cylinder127]
FEATURE [Part::Cut] Cut015  label="BowTie"
  Base = -> Box021
  Placement = pos=(-16.5,0,0) rot=(0,0,1;0rad)
  Tool = -> Fusion050
FEATURE [Part::Cylinder] Cylinder129  label="BowTieNozzle001"
  Angle = 360
  AttacherType = Attacher::AttachEngine3D
  Height = 10
  Placement = pos=(122,148.5,68) rot=(0,0,1;0rad)
  Radius = 0.4
FEATURE [Part::Cone] Cone
  Angle = 360
  AttacherType = Attacher::AttachEngine3D
  Height = 5
  Placement = pos=(122,148.5,70) rot=(0,0,1;0rad)
  Radius1 = 2.1
  Radius2 = 1
FEATURE [Part::Cylinder] Cylinder130  label="BowTieNozzle002"
  Angle = 360
  AttacherType = Attacher::AttachEngine3D
  Height = 2
  Placement = pos=(122,148.5,68) rot=(0,0,1;0rad)
  Radius = 2.1
FEATURE [Part::MultiFuse] Fusion051  label="BowTieNozzle"
  Shapes = -> [Cylinder130,Cone]
FEATURE [Part::Cut] Cut016  label="BowTieNozzle003"
  Base = -> Fusion051
  Placement = pos=(-16.5,0,0) rot=(0,0,1;0rad)
  Tool = -> Cylinder129
FEATURE [Part::Cylinder] Cylinder131  label="FT1bar001"
  Angle = 360
  AttacherType = Attacher::AttachEngine3D
  Height = 80
  Placement = pos=(73.66,148,-20) rot=(0,0,1;0rad)
  Radius = 12
FEATURE [Part::Cylinder] Cylinder132  label="FT1flange001"
  Angle = 360
  AttacherType = Attacher::AttachEngine3D
  Height = 3
  Placement = pos=(73.66,148,-8) rot=(0,0,1;0rad)
  Radius = 17
  expr: Placement.Base.x = 210.81999999999999 / 2 - 31.75
FEATURE [Part::MultiFuse] Fusion052  label="FT002"
  Placement = pos=(63.5,0,0) rot=(0,0,1;0rad)
  Shapes = -> [Cylinder131,Cylinder132]
  expr: Placement.Base.x = 137.16 - 73.659999999999997
FEATURE [Part::Cylinder] Cylinder133  label="BowTieBarRound2"
  Angle = 360
  AttacherType = Attacher::AttachEngine3D
  Height = 5
  Placement = pos=(137.16,148,60) rot=(0,0,1;0rad)
  Radius = 7
  expr: Placement.Base.x = 210.81999999999999 / 2 - 31.75 + 63.5
FEATURE [Part::Box] Box024  label="BowTieBar002"
  AttacherType = Attacher::AttachEngine3D
  Height = 5
  Length = 25.75
  Placement = pos=(111.41,143,60) rot=(0,0,1;0rad)
  Width = 10
  expr: Length = 63.5 / 2 - 10 + 4
  expr: Placement.Base.x = 73.659999999999997 + 63.5 - 25.75
FEATURE [Part::Cylinder] Cylinder134  label="BowTieBarMount1"
  Angle = 360
  AttacherType = Attacher::AttachEngine3D
  Height = 9
  Placement = pos=(137.16,148,63) rot=(0,0,1;0rad)
  Radius = 3.35
  expr: Radius = 6.7000000000000002 / 2
  expr: Placement.Base.x = 210.81999999999999 / 2 - 31.75 + 63.5
FEATURE [Part::MultiFuse] Fusion053
  Shapes = -> [Fusion003,Common,Cut001,Cylinder053,Fusion024,Fusion025,Fusion027,Fusion029,Cylinder067,Cylinder070,Cylinder072,Part__Feature005,Fusion040,Cylinder083,Cylinder082]
FEATURE [Part::Cut] Cut017
  Base = -> Box
  Tool = -> Fusion053
FEATURE [Part::Cylinder] Cylinder135  label="Cylinder007"
  Angle = 360
  AttacherType = Attacher::AttachEngine3D
  Height = 13.5
  Radius = 6.45
  expr: Radius = 12.9 / 2
FEATURE [Part::Cylinder] Cylinder136  label="BowTieNozzle004"
  Angle = 360
  AttacherType = Attacher::AttachEngine3D
  Height = 9
  Placement = pos=(122,148.5,69) rot=(0,0,1;0rad)
  Radius = 0.2
FEATURE [Part::Cone] Cone001
  Angle = 360
  AttacherType = Attacher::AttachEngine3D
  Height = 4
  Placement = pos=(122,148.5,70) rot=(0,0,1;0rad)
  Radius1 = 1
  Radius2 = 0.5
FEATURE [Part::Cylinder] Cylinder137  label="BowTieNozzle005"
  Angle = 360
  AttacherType = Attacher::AttachEngine3D
  Height = 1
  Placement = pos=(122,148.5,69) rot=(0,0,1;0rad)
  Radius = 1
FEATURE [Part::Cylinder] Cylinder138  label="BowTieNozzle007"
  Angle = 360
  AttacherType = Attacher::AttachEngine3D
  Height = 9
  Placement = pos=(121,148.5,69) rot=(0,1,0;1.5708rad)
  Radius = 0.4
FEATURE [Part::Cylinder] Cylinder139  label="BowTieNozzle008"
  Angle = 360
  AttacherType = Attacher::AttachEngine3D
  Height = 9
  Placement = pos=(121,148.5,69) rot=(0,1,0;1.5708rad)
  Radius = 0.7
FEATURE [Part::MultiFuse] Fusion054
  Shapes = -> [Box020,Cylinder116,Cylinder117,Fusion052,Cylinder133,Box024,Cylinder134,Fusion043]
FEATURE [Part::MultiFuse] Fusion055
  Shapes = -> [Cut016,Cut015]
FEATURE [Part::Feature] Part__Feature007  label="353-502"
  Placement = pos=(102,35,67) rot=(1,0,0;1.5708rad)
  shape: bbox 69.52 x 69.52 x 159.7 mm, 770 faces, 3 solids (baked)
